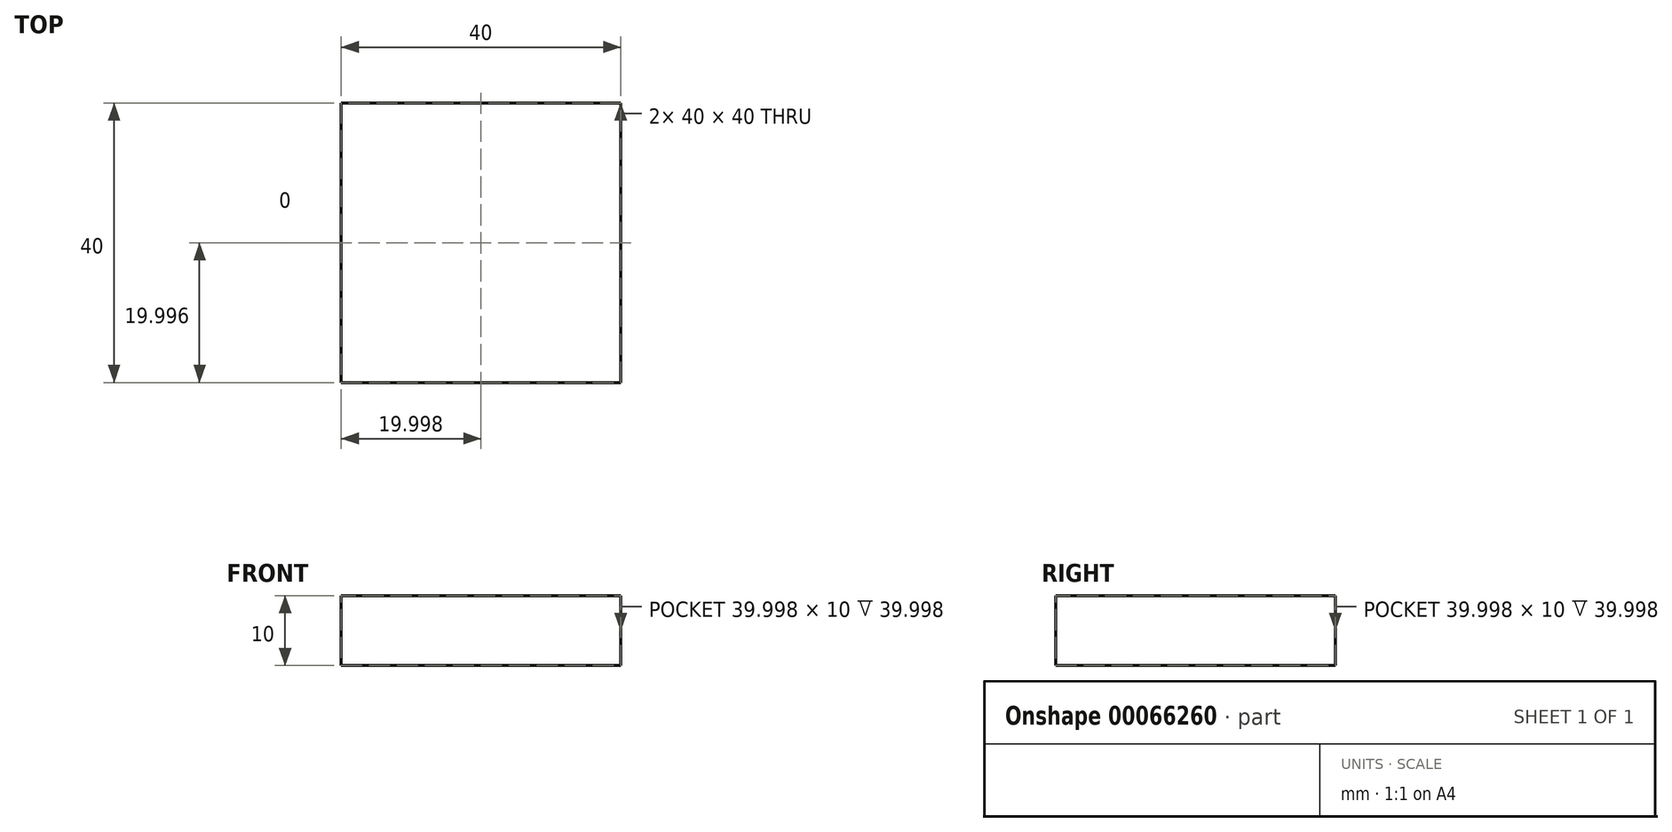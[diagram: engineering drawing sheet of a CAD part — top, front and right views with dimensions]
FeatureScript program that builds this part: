
annotation { "Feature Type Name" : "Feature", "Feature Type Description" : "" }
export const myFeature = defineFeature(function(context is Context, id is Id, definition is map)
    precondition{}
    {
        {
            var Q0;
            Q0=qCreatedBy(makeId("Top.planeOp"),FACE);
            var sketch = newSketch(context, id + "F0", { "sketchPlane" : qUnion([Q0])});
            skLineSegment(sketch, "E0.bottom", {"start": v(-38.4, 5) * mm, "end": v(1.6, 5) * mm});
            skLineSegment(sketch, "E0.top", {"start": v(-38.4, -35) * mm, "end": v(1.6, -35) * mm});
            skLineSegment(sketch, "E0.left", {"start": v(-38.4, 5) * mm, "end": v(-38.4, -35) * mm});
            skLineSegment(sketch, "E0.right", {"start": v(1.6, 5) * mm, "end": v(1.6, -35) * mm});
            skSolve(sketch);
        }
        {
            var Q0;
            Q0=makeQuery(id+"F0.imprint","IMPRINT",FACE,{"disambiguationData":[TD([[makeQuery(id+"F0.imprint","IMPRINT",EDGE,{"derivedFrom":sQuery(id+"F0.wireOp",EDGE,"E0.bottom")}),-1.0]])]});
            extrude(context, id + "F1", {"entities" : qUnion([Q0]), "depth" : 10 * mm});
        }
    });
